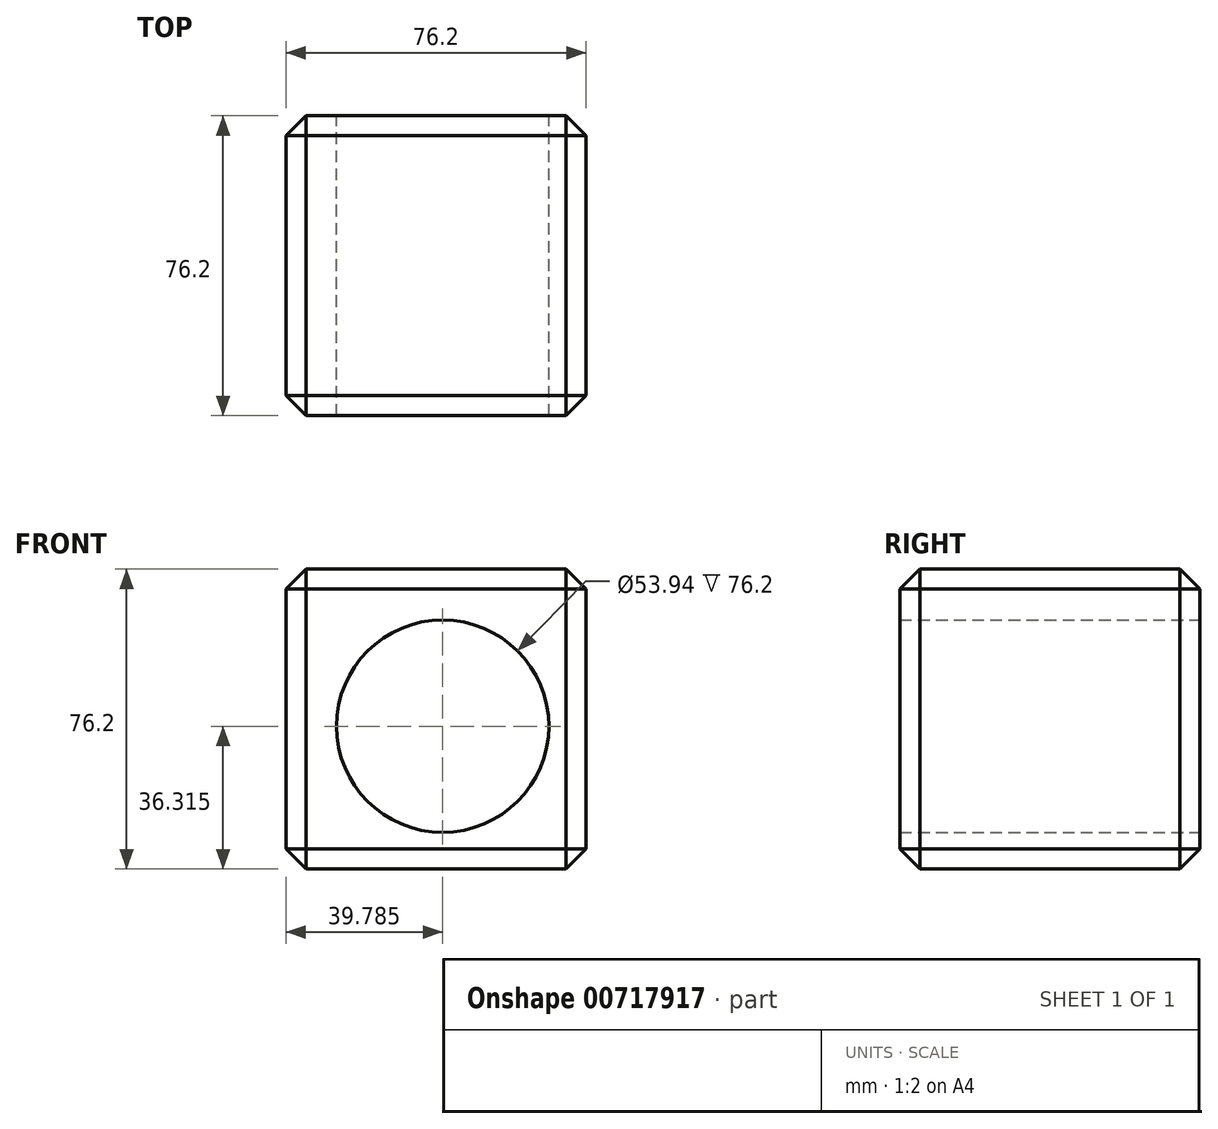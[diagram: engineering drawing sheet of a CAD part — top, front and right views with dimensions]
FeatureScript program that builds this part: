
annotation { "Feature Type Name" : "Feature", "Feature Type Description" : "" }
export const myFeature = defineFeature(function(context is Context, id is Id, definition is map)
    precondition{}
    {
        {
            var Q0;
            Q0=qCreatedBy(makeId("Front.planeOp"),FACE);
            var sketch = newSketch(context, id + "F0", { "sketchPlane" : qUnion([Q0])});
            skLineSegment(sketch, "E0.bottom", {"start": v(-37.89, 37.42) * mm, "end": v(38.31, 37.42) * mm});
            skLineSegment(sketch, "E0.top", {"start": v(-37.89, -38.78) * mm, "end": v(38.31, -38.78) * mm});
            skLineSegment(sketch, "E0.left", {"start": v(-37.89, 37.42) * mm, "end": v(-37.89, -38.78) * mm});
            skLineSegment(sketch, "E0.right", {"start": v(38.31, 37.42) * mm, "end": v(38.31, -38.78) * mm});
            skSolve(sketch);
        }
        {
            var Q0;
            Q0=makeQuery(id+"F0.imprint","IMPRINT",FACE,{"disambiguationData":[TD([[makeQuery(id+"F0.imprint","IMPRINT",EDGE,{"derivedFrom":sQuery(id+"F0.wireOp",EDGE,"E0.bottom")}),-1.0]])]});
            extrude(context, id + "F1", {"entities" : qUnion([Q0]), "depth" : 76.2 * mm, "offsetDistance" : 25.4 * mm});
        }
        {
            var Q0;
            Q0=makeQuery(id+"F1.opExtrude","CAP_FACE",FACE,{"disambiguationData":[OSD([sQuery(id+"F0.wireOp",EDGE,"E0.bottom"),sQuery(id+"F0.wireOp",EDGE,"E0.top"),sQuery(id+"F0.wireOp",EDGE,"E0.left"),sQuery(id+"F0.wireOp",EDGE,"E0.right")])],"isStart":true});
            var sketch = newSketch(context, id + "F2", { "sketchPlane" : qUnion([Q0])});
            skCircle(sketch, "E1", {"center": v(-1.9, -2.46) * mm, "radius": 26.97 * mm});
            skSolve(sketch);
        }
        {
            var Q0;
            Q0=makeQuery(id+"F2.imprint","IMPRINT",FACE,{"disambiguationData":[TD([[makeQuery(id+"F2.imprint","IMPRINT",EDGE,{"derivedFrom":sQuery(id+"F2.wireOp",EDGE,"E1")}),1.0]])]});
            extrude(context, id + "F3", {"entities" : qUnion([Q0]), "operationType" : NewBodyOperationType.REMOVE, "endBound" : BoundingType.THROUGH_ALL, "oppositeDirection" : true, "depth" : 76.2 * mm, "offsetDistance" : 25.4 * mm});
        }
        {
            var Q0;
            Q0=makeQuery(id+"F1.opExtrude","SWEPT_FACE",FACE,{"disambiguationData":[OSD([sQuery(id+"F0.wireOp",EDGE,"E0.left")])]});
            var Q1;
            Q1=makeQuery(id+"F1.opExtrude","SWEPT_FACE",FACE,{"disambiguationData":[OSD([sQuery(id+"F0.wireOp",EDGE,"E0.top")])]});
            var Q2;
            Q2=makeQuery(id+"F1.opExtrude","SWEPT_FACE",FACE,{"disambiguationData":[OSD([sQuery(id+"F0.wireOp",EDGE,"E0.right")])]});
            var Q3;
            Q3=makeQuery(id+"F1.opExtrude","SWEPT_FACE",FACE,{"disambiguationData":[OSD([sQuery(id+"F0.wireOp",EDGE,"E0.bottom")])]});
            chamfer(context, id + "F4", {"entities" : qUnion([Q0, Q1, Q2, Q3]), "width" : 5.08 * mm, "tangentPropagation" : true});
        }
    });
